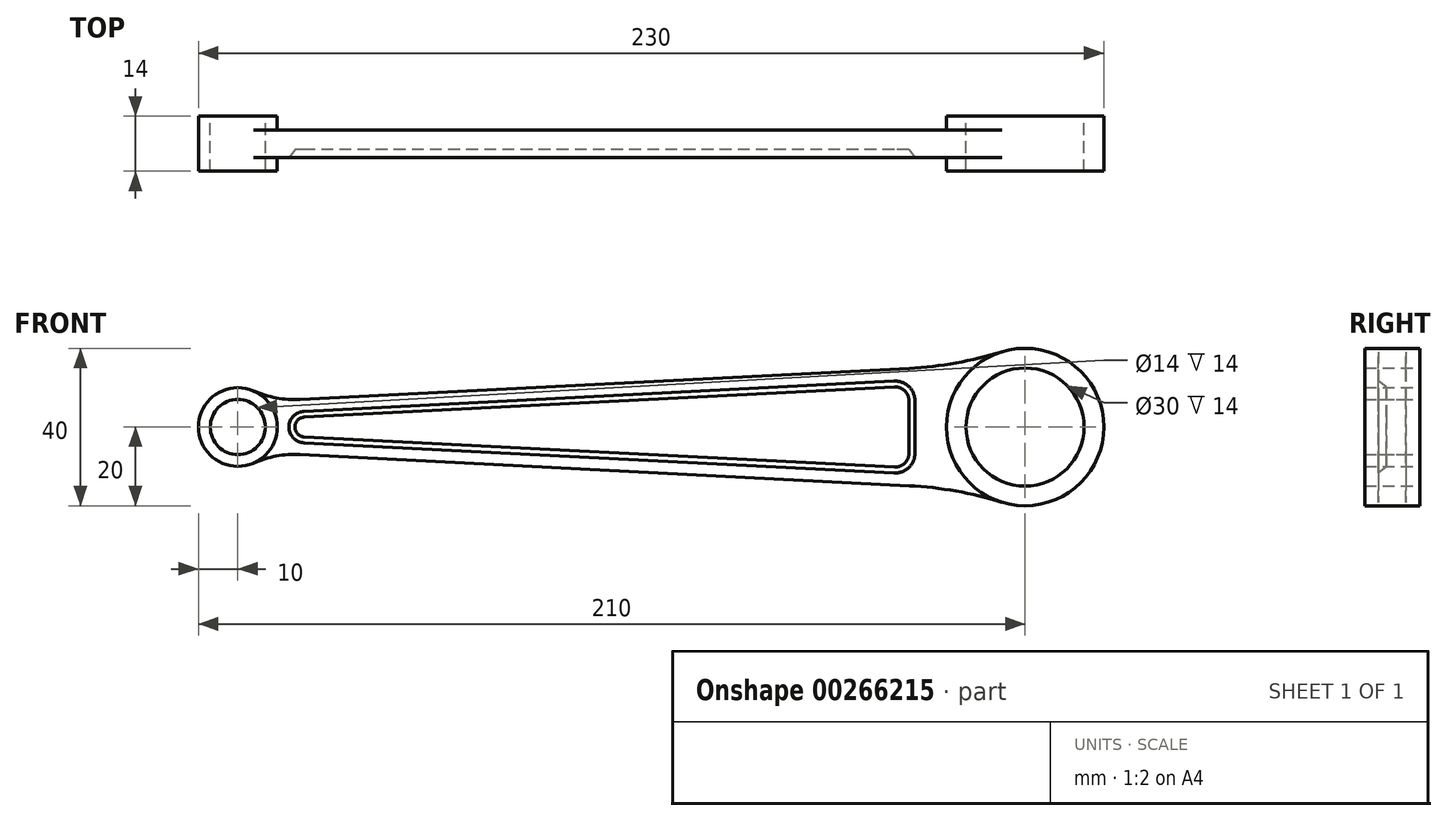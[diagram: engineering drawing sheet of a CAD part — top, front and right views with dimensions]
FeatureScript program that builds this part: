
annotation { "Feature Type Name" : "Feature", "Feature Type Description" : "" }
export const myFeature = defineFeature(function(context is Context, id is Id, definition is map)
    precondition{}
    {
        {
            var Q0;
            Q0=qCreatedBy(makeId("Front.planeOp"),FACE);
            var sketch = newSketch(context, id + "F0", { "sketchPlane" : qUnion([Q0])});
            skCircle(sketch, "E0", {"center": v(0, 0) * mm, "radius": 10 * mm});
            skCircle(sketch, "E1", {"center": v(0, 0) * mm, "radius": 7 * mm});
            skCircle(sketch, "E2", {"center": v(200, 0) * mm, "radius": 20 * mm});
            skCircle(sketch, "E3", {"center": v(200, 0) * mm, "radius": 15 * mm});
            skPoint(sketch, "E4.orphan", {"position": v(37.25, 85.18) * mm});
            skPoint(sketch, "E5.orphan", {"position": v(37.25, -85.18) * mm});
            skPoint(sketch, "E6.end.orphan", {"position": v(4.02, 9.16) * mm});
            skPoint(sketch, "E6.start.orphan", {"position": v(-23.56, 8) * mm});
            skPoint(sketch, "E7.MirrorCS.end.orphan", {"position": v(4.02, -9.16) * mm});
            skPoint(sketch, "E7.MirrorCS.start.orphan", {"position": v(-23.56, -8) * mm});
            skPoint(sketch, "E8.MirrorCS.end.orphan", {"position": v(180.7, -5.26) * mm});
            skPoint(sketch, "E9.end.orphan", {"position": v(180.7, 5.26) * mm});
            skLineSegment(sketch, "E10", {"start": v(15.8, 7) * mm, "end": v(170.6, 14.93) * mm});
            skArc(sketch, "E11", {"start": v(15.8, 7) * mm, "mid": v(9.78, 7.4) * mm, "end": v(4.02, 9.16) * mm});
            skArc(sketch, "E12", {"start": v(170.6, 14.93) * mm, "mid": v(182.47, 16.29) * mm, "end": v(194.08, 19.1) * mm});
            skLineSegment(sketch, "E13.MirrorCS", {"start": v(15.8, -7) * mm, "end": v(170.6, -14.93) * mm});
            skArc(sketch, "E14.MirrorCS", {"start": v(170.6, -14.93) * mm, "mid": v(182.47, -16.29) * mm, "end": v(194.08, -19.1) * mm});
            skArc(sketch, "E15.MirrorCS", {"start": v(15.8, -7) * mm, "mid": v(9.78, -7.4) * mm, "end": v(4.02, -9.16) * mm});
            skSolve(sketch);
        }
        {
            var Q0;
            Q0=qCreatedBy(makeId("Front.planeOp"),FACE);
            cPlane(context, id + "F1", {"entities" : qUnion([Q0]), "cplaneType" : CPlaneType.OFFSET, "offset" : 1.5 * mm, "width" : 150 * mm, "height" : 150 * mm});
        }
        {
            var Q0;
            Q0=makeQuery(id+"F0.imprint","IMPRINT",FACE,{"disambiguationData":[TD([[makeQuery(id+"F0.imprint","IMPRINT",EDGE,{"derivedFrom":sQuery(id+"F0.wireOp",EDGE,"E10")}),-1.0]])]});
            extrude(context, id + "F2", {"entities" : qUnion([Q0]), "endBound" : BoundingType.SYMMETRIC, "depth" : 7 * mm});
        }
        {
            var Q0;
            Q0=makeQuery(id+"F0.imprint","IMPRINT",FACE,{"disambiguationData":[TD([[makeQuery(id+"F0.imprint","IMPRINT",EDGE,{"derivedFrom":sQuery(id+"F0.wireOp",EDGE,"E3")}),-1.0]])]});
            var Q1;
            Q1=makeQuery(id+"F0.imprint","IMPRINT",FACE,{"disambiguationData":[TD([[makeQuery(id+"F0.imprint","IMPRINT",EDGE,{"derivedFrom":sQuery(id+"F0.wireOp",EDGE,"E1")}),-1.0]])]});
            extrude(context, id + "F3", {"entities" : qUnion([Q0, Q1]), "operationType" : NewBodyOperationType.ADD, "endBound" : BoundingType.SYMMETRIC, "depth" : 14 * mm});
        }
        {
            var Q0;
            Q0=makeQuery(id+"F2.opExtrude","CAP_FACE",FACE,{"disambiguationData":[OSD([sQuery(id+"F0.wireOp",EDGE,"E0"),sQuery(id+"F0.wireOp",EDGE,"E2"),sQuery(id+"F0.wireOp",EDGE,"E10"),sQuery(id+"F0.wireOp",EDGE,"E11"),sQuery(id+"F0.wireOp",EDGE,"E12"),sQuery(id+"F0.wireOp",EDGE,"E13.MirrorCS"),sQuery(id+"F0.wireOp",EDGE,"E14.MirrorCS"),sQuery(id+"F0.wireOp",EDGE,"E15.MirrorCS")])],"isStart":false});
            var sketch = newSketch(context, id + "F4", { "sketchPlane" : qUnion([Q0])});
            skLineSegment(sketch, "E16", {"start": v(16.8, 4) * mm, "end": v(166.74, 11.68) * mm});
            skLineSegment(sketch, "E17", {"start": v(172, 6.69) * mm, "end": v(172, -6.69) * mm});
            skLineSegment(sketch, "E18.MirrorCS", {"start": v(16.8, -4) * mm, "end": v(166.74, -11.68) * mm});
            skArc(sketch, "E19", {"start": v(16.8, 4) * mm, "mid": v(13, 0) * mm, "end": v(16.8, -4) * mm});
            skPoint(sketch, "E20.visualSharp", {"position": v(172, 11.95) * mm});
            skArc(sketch, "E20.filletArc", {"start": v(172, 6.69) * mm, "mid": v(170.44, 10.31) * mm, "end": v(166.74, 11.68) * mm});
            skPoint(sketch, "E21.visualSharp", {"position": v(172, -11.95) * mm});
            skArc(sketch, "E21.filletArc", {"start": v(166.74, -11.68) * mm, "mid": v(170.44, -10.31) * mm, "end": v(172, -6.69) * mm});
            skSolve(sketch);
        }
        {
            var Q0;
            Q0=qCreatedBy(id+"F1.planeOp",FACE);
            var sketch = newSketch(context, id + "F5", { "sketchPlane" : qUnion([Q0])});
            skArc(sketch, "E22.0", {"start": v(16.87, 2.5) * mm, "mid": v(14.5, 0) * mm, "end": v(16.87, -2.5) * mm});
            skArc(sketch, "E22.1", {"start": v(166.82, -10.18) * mm, "mid": v(169.41, -9.22) * mm, "end": v(170.5, -6.69) * mm});
            skLineSegment(sketch, "E22.2", {"start": v(170.5, -6.69) * mm, "end": v(170.5, 6.69) * mm});
            skLineSegment(sketch, "E22.3", {"start": v(16.87, -2.5) * mm, "end": v(166.82, -10.18) * mm});
            skArc(sketch, "E22.4", {"start": v(170.5, 6.69) * mm, "mid": v(169.41, 9.22) * mm, "end": v(166.82, 10.18) * mm});
            skLineSegment(sketch, "E22.5", {"start": v(166.82, 10.18) * mm, "end": v(16.87, 2.5) * mm});
            skSolve(sketch);
        }
        {
            var Q1;
            Q1 = qSketchRegion(id + "F5", true);
            var Q2;
            Q2 = qSketchRegion(id + "F4", true);
            loft(context, id + "F6", {"operationType" : NewBodyOperationType.REMOVE, "sheetProfilesArray" : [{ "sheetProfileEntities" : qUnion([Q1]) }, { "sheetProfileEntities" : qUnion([Q2]) }]});
        }
    });
